# Revit family: Access_Door-Acudor-Fire_Rated_Insulated-FW-5050-UP_Series
name_source: partatom
category: Specialty Equipment
revit_build: Autodesk Revit 2014 (Build: 20130308_1515(x64)
units: mm (PartAtom-declared; Revit-internal decimal feet)

## types (4) — shared parameters
Assembly Code = C1020700
Default Elevation = 0"
Description = Fire Rated, Insulated Access Door for Ceilings
Finish = Stainless Steel-Acudor-20 Gauge-Satin
Installation Type = Ceiling Mounted
L-Handle = Yes
Length = 3 3/16"
Manufacturer = Acudor
Material = Stainless Steel-Acudor-20 Gauge-Satin
Product Documentation Link = https://www.acudor.com
Product Page URL = https://www.acudor.com
Revised Date = 08/28/2018
Rim Cylinder Lock = No
URL = http://acudor.com

## per-type parameters (varying)
| type | 1 Latch | 2 Latches | Height | Width |
| FW-5050-UP 22x30 | No | Yes | 30" | 22" |
| FW-5050-UP 22x36 | No | Yes | 30" | 22" |
| FW-5050-UP 24x24 | Yes | No | 24" | 24" |
| FW-5050-UP 24x36 | No | Yes | 36" | 24" |

note: column(s) folded — value = type name in every type: Model

## geometry (parser evidence)
native form markers: Sweep x2
no freeform markers — native parametric forms only
